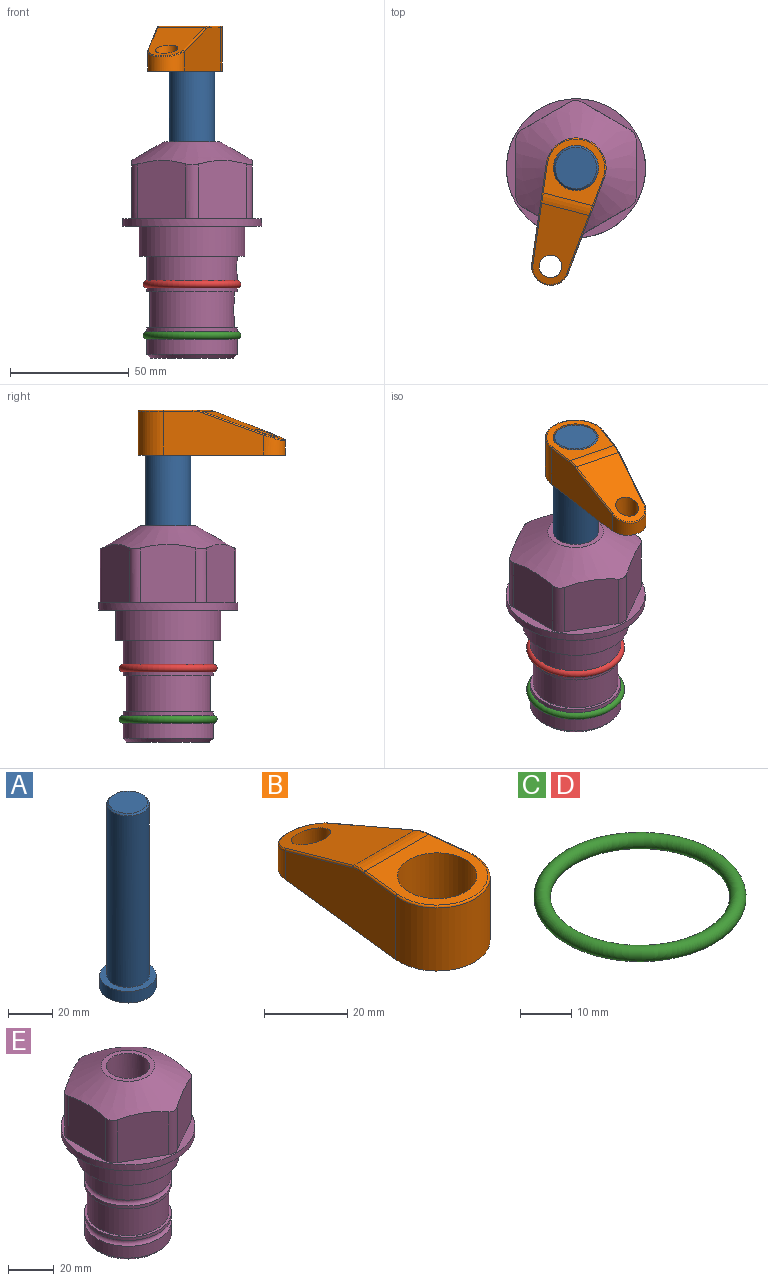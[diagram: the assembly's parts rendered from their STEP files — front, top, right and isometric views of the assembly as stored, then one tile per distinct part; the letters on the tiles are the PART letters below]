
ASSEMBLY  parts=5 mates=3
PART A: 6 faces, bbox 25.4x25.4x101.6 mm
  f0: plane 17.46x17.46mm, normal (0,0,1), area 239.5mm2, adj f5
  f1: plane 25.4x25.4mm, normal (0,0,-1), area 506.7mm2, adj f2
  f2: cylinder r=12.7mm len=25.4mm, axis (0,0,1), area 506.7mm2, adj f1,f3
  f3: plane 25.4x25.4mm, normal (0,0,1), area 221.7mm2, adj f2,f4
  f4: cylinder r=9.53mm len=94.46mm, axis (0,0,1), area 5653mm2, adj f3,f5
  f5: cone r=8.73mm half-angle=45deg, axis (0,0,-1), area 64.4mm2, adj f0,f4
PART B: 44 faces, bbox 27.5x64.5x19.1 mm
  f0: plane 2.3x0.95mm, normal (0,0,-1), area 1mm2, adj f25,f30,f34
  f1: plane 63.5x25.4mm, normal (0,0,-1), area 561.7mm2, adj f2,f3,f4,f5,f6,f7,f19,f20
  f2: cylinder r=12.7mm len=25.4mm, axis (0,0,-1), area 792.2mm2, adj f1,f3,f5,f13
  f3: plane 42.33x18.54mm, normal (0.99,0.11,0), area 647mm2, adj f1,f2,f4,f11,f12,f14
  f4: cylinder r=7.94mm len=15.78mm, axis (0,0,-1), area 158.6mm2, adj f1,f3,f5,f16
  f5: plane 42.33x18.54mm, normal (-0.99,0.11,0), area 647mm2, adj f1,f2,f4,f15,f17,f18
  f6: cylinder r=9.53mm len=19.05mm, axis (0,0,-1), area 1140.1mm2, adj f1,f8
  f7: cylinder r=4.76mm len=10.98mm, axis (0,0,-1), area 276.1mm2, adj f1,f9
  f8: plane 25.83x24.38mm, normal (0,0,1), area 262.2mm2, adj f6,f10,f11,f13,f15
  f9: plane 32.49x20.55mm, normal (0,0.34,0.94), area 489.9mm2, adj f7,f10,f14,f16,f18
  f10: cylinder r=12.7mm len=21.49mm, axis (-1,0,0), area 93.2mm2, adj f8,f9,f12,f17
  f11: cylinder r=0.51mm len=12.34mm, axis (0.11,-0.99,0), area 9.9mm2, adj f3,f8,f12,f13
  f12: bspline ~7.62x1.64mm, area 3.5mm2, adj f3,f10,f11,f14
  f13: torus R=12.19mm, axis (0,0,1), area 33.6mm2, adj f2,f8,f11,f15
  f14: cylinder r=0.51mm len=26.01mm, axis (0.1,-0.93,0.34), area 21.6mm2, adj f3,f9,f12,f16
  f15: cylinder r=0.51mm len=12.34mm, axis (0.11,0.99,0), area 9.9mm2, adj f5,f8,f13,f17
  f16: bspline ~15.78x7.05mm, area 15.7mm2, adj f4,f9,f14,f18
  f17: bspline ~7.62x1.64mm, area 3.5mm2, adj f5,f10,f15,f18
  f18: cylinder r=0.51mm len=26.01mm, axis (0.1,0.93,-0.34), area 21.6mm2, adj f5,f9,f16,f17
  f19: plane 21.6x14.29mm, normal (-0.99,-0.11,0), area 242.6mm2, adj f1,f26,f28,f34,f36,f38
  f20: plane 21.6x14.29mm, normal (0.99,-0.11,0), area 242.6mm2, adj f1,f27,f29,f37,f39,f41
  f21: cylinder r=12.7mm len=14.29mm, axis (0,0,-1), area 173.2mm2, adj f1,f26,f27,f30,f31,f33
  f22: cylinder r=7.94mm len=7.63mm, axis (0,0,-1), area 53.8mm2, adj f1,f28,f29,f42
  f23: plane 2.3x0.95mm, normal (0,0,-1), area 1mm2, adj f25,f33,f37
  f24: plane 17.94x12.32mm, normal (0,-0.34,-0.94), area 191.2mm2, adj f25,f38,f41,f42
  f25: cylinder r=9.53mm len=12.93mm, axis (-1,0,0), area 37.5mm2, adj f0,f23,f24,f31,f36,f39
  f26: cylinder r=1.59mm len=14.29mm, axis (0,0,-1), area 49mm2, adj f1,f19,f21,f32
  f27: cylinder r=1.59mm len=14.29mm, axis (0,0,-1), area 49mm2, adj f1,f20,f21,f35
  f28: cylinder r=1.59mm len=7.28mm, axis (0,0,-1), area 22.1mm2, adj f1,f19,f22,f40
  f29: cylinder r=1.59mm len=7.28mm, axis (0,0,-1), area 22.1mm2, adj f1,f20,f22,f43
  f30: torus R=14.29mm, axis (0,0,1), area 5.8mm2, adj f0,f21,f31,f32
  f31: bspline ~11.06x2.73mm, area 20.8mm2, adj f21,f25,f30,f33
  f32: sphere r=1.59mm, area 5.4mm2, adj f26,f30,f34
  f33: torus R=14.29mm, axis (0,0,1), area 5.8mm2, adj f21,f23,f31,f35
  f34: cylinder r=1.59mm len=1.68mm, axis (-0.11,0.99,0), area 2.4mm2, adj f0,f19,f32,f36
  f35: sphere r=1.59mm, area 5.4mm2, adj f27,f33,f37
  f36: bspline ~5.82x2.33mm, area 7.7mm2, adj f19,f25,f34,f38
  f37: cylinder r=1.59mm len=1.68mm, axis (0.11,0.99,0), area 2.4mm2, adj f20,f23,f35,f39
  f38: cylinder r=1.59mm len=18.33mm, axis (0.1,-0.93,0.34), area 46.7mm2, adj f19,f24,f36,f40
  f39: bspline ~5.82x2.33mm, area 7.7mm2, adj f20,f25,f37,f41
  f40: sphere r=1.59mm, area 3.6mm2, adj f28,f38,f42
  f41: cylinder r=1.59mm len=18.33mm, axis (0.1,0.93,-0.34), area 46.7mm2, adj f20,f24,f39,f43
  f42: bspline ~8.31x1.84mm, area 15.3mm2, adj f22,f24,f40,f43
  f43: sphere r=1.59mm, area 3.6mm2, adj f29,f41,f42
PART C: 1 faces, bbox 44.7x44.7x3.2 mm
  f0: torus R=19.05mm, axis (0,0,1), area 1193.9mm2
PART D: same geometry as C
PART E: 36 faces, bbox 58.7x58.7x91.2 mm
  f0: cylinder r=17.78mm len=35.56mm, axis (0,0,1), area 1670.8mm2, adj f23,f24,f31
  f1: cylinder r=19.05mm len=38.1mm, axis (0,0,1), area 1191.9mm2, adj f26,f27,f30
  f2: plane 58.66x58.66mm, normal (0,0,-1), area 1150.6mm2, adj f3,f28
  f3: cylinder r=29.33mm len=58.66mm, axis (0,0,-1), area 585.1mm2, adj f2,f4
  f4: plane 58.66x58.66mm, normal (0,0,1), area 475.9mm2, adj f3,f5,f6,f7,f8,f9,f10,f11
  f5: plane 24.5x20.32mm, normal (-0.5,0.87,0), area 562.8mm2, adj f4,f15,f16,f17
  f6: plane 24.5x20.32mm, normal (0.5,0.87,0), area 562.8mm2, adj f4,f14,f15,f17
  f7: plane 24.5x23.48mm, normal (1,0,0), area 562.8mm2, adj f4,f13,f14,f17
  f8: plane 24.5x20.32mm, normal (0.5,-0.87,0), area 562.8mm2, adj f4,f12,f13,f17
  f9: plane 24.5x20.32mm, normal (-0.5,-0.87,0), area 562.8mm2, adj f4,f11,f12,f17
  f10: plane 24.5x23.48mm, normal (-1,0,0), area 562.8mm2, adj f4,f11,f16,f17
  f11: cylinder r=5.08mm len=23.01mm, axis (0,0,-1), area 121.2mm2, adj f4,f9,f10,f17
  f12: cylinder r=5.08mm len=23.01mm, axis (0,0,-1), area 121.2mm2, adj f4,f8,f9,f17
  f13: cylinder r=5.08mm len=23.01mm, axis (0,0,-1), area 121.2mm2, adj f4,f7,f8,f17
  f14: cylinder r=5.08mm len=23.01mm, axis (0,0,-1), area 121.2mm2, adj f4,f6,f7,f17
  f15: cylinder r=5.08mm len=23.01mm, axis (0,0,-1), area 121.2mm2, adj f4,f5,f6,f17
  f16: cylinder r=5.08mm len=23.01mm, axis (0,0,-1), area 121.2mm2, adj f4,f5,f10,f17
  f17: cone r=11.73mm half-angle=60deg, axis (0,0,-1), area 2071.8mm2, adj f5,f6,f7,f8,f9,f10,f11,f12
  f18: plane 23.46x23.46mm, normal (0,0,1), area 147.4mm2, adj f17,f35
  f19: plane 34.93x34.93mm, normal (0,0,-1), area 958mm2, adj f29
  f20: cylinder r=19.05mm len=38.1mm, axis (0,0,1), area 760.1mm2, adj f21,f29
  f21: torus R=19.05mm, axis (0,0,1), area 565.3mm2, adj f20,f22
  f22: cylinder r=19.05mm len=38.1mm, axis (0,0,1), area 190mm2, adj f21,f23
  f23: plane 38.1x38.1mm, normal (0,0,1), area 146.9mm2, adj f0,f22
  f24: plane 38.1x38.1mm, normal (0,0,-1), area 146.9mm2, adj f0,f25
  f25: cylinder r=19.05mm len=38.1mm, axis (0,0,1), area 190mm2, adj f24,f26
  f26: torus R=19.05mm, axis (0,0,1), area 565.3mm2, adj f1,f25
  f27: plane 44.45x44.45mm, normal (0,0,-1), area 411.7mm2, adj f1,f28
  f28: cylinder r=22.23mm len=44.45mm, axis (0,0,1), area 1773.5mm2, adj f2,f27
  f29: cone r=19.05mm half-angle=45deg, axis (0,0,1), area 257.5mm2, adj f19,f20
  f30: cylinder r=3.17mm len=6.75mm, axis (-1,0,0), area 128mm2, adj f1,f33
  f31: cylinder r=3.17mm len=6.35mm, axis (-1,0,0), area 102.5mm2, adj f0,f33
  f32: plane 25.4x25.4mm, normal (0,0,1), area 506.7mm2, adj f33
  f33: cylinder r=12.7mm len=66.42mm, axis (0,0,-1), area 5236.2mm2, adj f30,f31,f32,f34
  f34: cone r=9.53mm half-angle=30deg, axis (0,0,-1), area 443.4mm2, adj f33,f35
  f35: cylinder r=9.53mm len=19.05mm, axis (0,0,-1), area 849mm2, adj f18,f34
PLACE A rot(axis=(0,0,-1),104.5deg) t=(0,0,10.69)mm
PLACE B rot(axis=(0,0,1),165.5deg) t=(0,0,65.3)mm
PLACE C t=(0,0,-21.59)mm
PLACE D at identity
PLACE E at identity fixed
MATE fastened C.f0 <-> E.f0  axis (0,0,1) through (0,0,-46.1)mm
MATE cylindrical A.f2 <-> E.f0  axis (0,0,1) through (0,0,36.33)mm
MATE fastened B.f2 <-> A.f2  axis (0,0,1) through (0,0,84.35)mm
